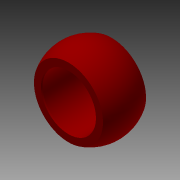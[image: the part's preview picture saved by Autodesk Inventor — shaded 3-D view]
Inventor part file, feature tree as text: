
AUTODESK INVENTOR PART (.ipt)
format: ipt  version: 2014 (Build 180170000, 170)  size: 114,176 bytes
history: native  units: mm (DEFAULTED — no unit token found)
features: sketch x2, revolve x1, extrude x1, hole x1, chamfer x1
ambient origin geometry x8: Origin, YZ Plane, XZ Plane, XY Plane, X Axis, Y Axis, Z Axis, Center Point
bodies: Solid1 (feature_tree)
feature tree (6):
  revolve  "Revolution1"  Angle=90.0deg
  extrude  "Extrusion3"  Depth=6.35mm TaperAngle=0.0deg
  hole  "Hole1"  [1 undecoded]
  chamfer  "Chamfer1"  Distance=0.3048mm Angle=30.0deg
  sketch  "Sketch1"  dims[d0=24.003mm d1=90.0deg]
  sketch  "Sketch4"  dims[d8=12.7mm d9=25.4mm d10=0.0mm d11=25.4mm d12=25.4mm d13=15.875mm d14=12.7mm d15=9.525mm d16=6.35mm d17=14.3117mm d18=19.05mm d19=20.594885mm d20=0.3048mm d21=3.175mm d22=30.0deg]
note: 1 required parameter value undecoded (feature->parameter linkage not recoverable at this tier; creation-order binding heuristic only, values carry confidence <= 0.55)
